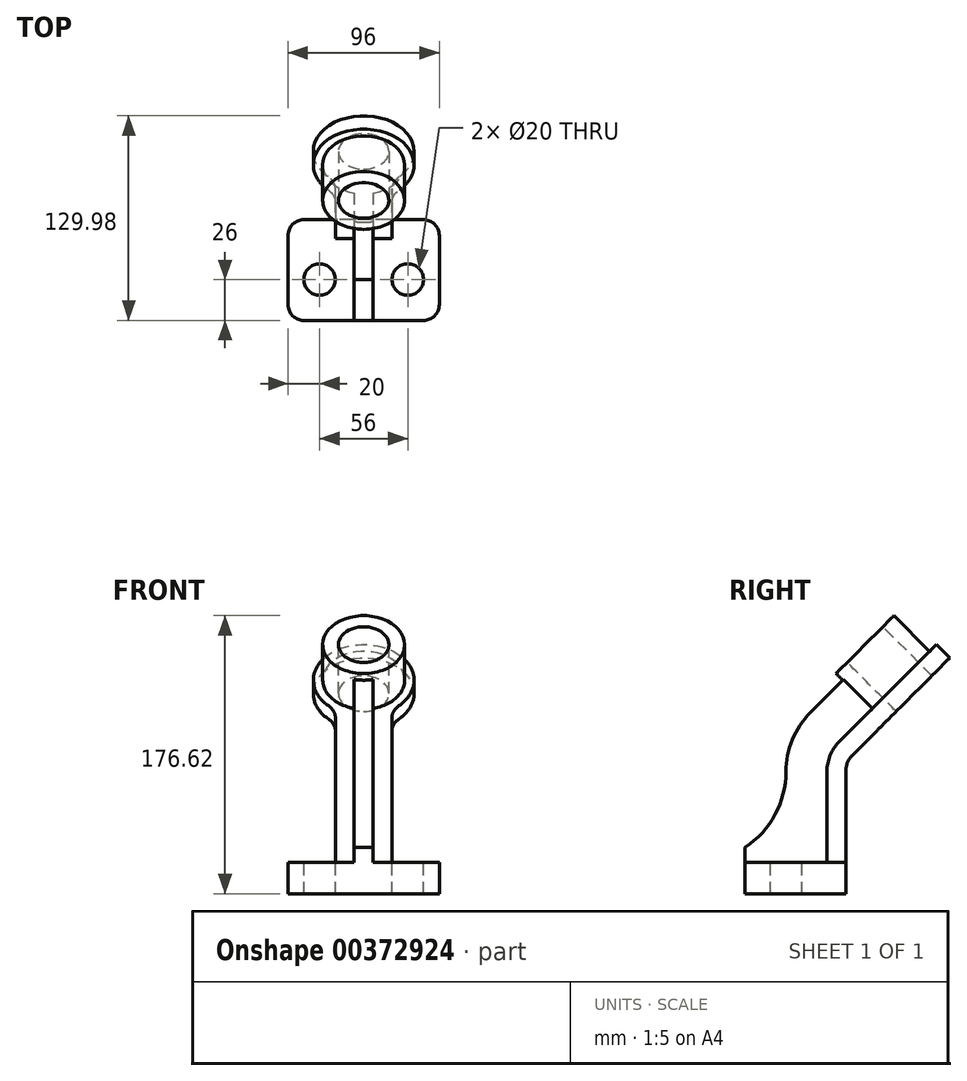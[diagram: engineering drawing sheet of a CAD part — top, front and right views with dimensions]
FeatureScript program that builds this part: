
annotation { "Feature Type Name" : "Feature", "Feature Type Description" : "" }
export const myFeature = defineFeature(function(context is Context, id is Id, definition is map)
    precondition{}
    {
        {
            var Q0;
            Q0=qCreatedBy(makeId("Top.planeOp"),FACE);
            var sketch = newSketch(context, id + "F0", { "sketchPlane" : qUnion([Q0])});
            skLineSegment(sketch, "E0.bottom", {"start": v(48, -32) * mm, "end": v(-48, -32) * mm});
            skLineSegment(sketch, "E0.top", {"start": v(48, 32) * mm, "end": v(-48, 32) * mm});
            skLineSegment(sketch, "E0.left", {"start": v(48, -32) * mm, "end": v(48, 32) * mm});
            skLineSegment(sketch, "E0.right", {"start": v(-48, -32) * mm, "end": v(-48, 32) * mm});
            skPoint(sketch, "E0.middle", {"position": v(0, 0) * mm});
            skSolve(sketch);
        }
        {
            var Q0;
            Q0=makeQuery(id+"F0.imprint","IMPRINT",FACE,{"disambiguationData":[TD([[makeQuery(id+"F0.imprint","IMPRINT",EDGE,{"derivedFrom":sQuery(id+"F0.wireOp",EDGE,"E0.bottom")}),-1.0]])]});
            extrude(context, id + "F1", {"entities" : qUnion([Q0]), "depth" : 20 * mm});
        }
        {
            var Q0;
            Q0=makeQuery(id+"F1.opExtrude","CAP_FACE",FACE,{"disambiguationData":[OSD([sQuery(id+"F0.wireOp",EDGE,"E0.bottom"),sQuery(id+"F0.wireOp",EDGE,"E0.top"),sQuery(id+"F0.wireOp",EDGE,"E0.left"),sQuery(id+"F0.wireOp",EDGE,"E0.right")])],"isStart":false});
            var sketch = newSketch(context, id + "F2", { "sketchPlane" : qUnion([Q0])});
            skCircle(sketch, "E1", {"center": v(-28, -6) * mm, "radius": 10 * mm});
            skCircle(sketch, "E2.MirrorC", {"center": v(28, -6) * mm, "radius": 10 * mm});
            skSolve(sketch);
        }
        {
            var Q0;
            Q0 = qSketchRegion(id + "F2", true);
            extrude(context, id + "F3", {"entities" : qUnion([Q0]), "operationType" : NewBodyOperationType.REMOVE, "oppositeDirection" : true, "depth" : 25 * mm});
        }
        {
            var Q0;
            Q0=makeQuery(id+"F1.opExtrude","SWEPT_EDGE",EDGE,{"disambiguationData":[OSD([sQuery(id+"F0.wireOp",EDGE,"E0.bottom"),sQuery(id+"F0.wireOp",EDGE,"E0.left")])]});
            var Q1;
            Q1=makeQuery(id+"F1.opExtrude","SWEPT_EDGE",EDGE,{"disambiguationData":[OSD([sQuery(id+"F0.wireOp",EDGE,"E0.bottom"),sQuery(id+"F0.wireOp",EDGE,"E0.right")])]});
            fillet(context, id + "F4", {"entities" : qUnion([Q0, Q1]), "radius" : 10 * mm, "tangentPropagation" : true, "allowEdgeOverflow" : false});
        }
        {
            var Q0;
            Q0=makeQuery(id+"F1.opExtrude","SWEPT_EDGE",EDGE,{"disambiguationData":[OSD([sQuery(id+"F0.wireOp",EDGE,"E0.top"),sQuery(id+"F0.wireOp",EDGE,"E0.right")])]});
            var Q1;
            Q1=makeQuery(id+"F1.opExtrude","SWEPT_EDGE",EDGE,{"disambiguationData":[OSD([sQuery(id+"F0.wireOp",EDGE,"E0.top"),sQuery(id+"F0.wireOp",EDGE,"E0.left")])]});
            fillet(context, id + "F5", {"entities" : qUnion([Q0, Q1]), "radius" : 10 * mm, "tangentPropagation" : true, "allowEdgeOverflow" : false});
        }
        {
            var Q0;
            Q0=qCreatedBy(makeId("Right.planeOp"),FACE);
            var sketch = newSketch(context, id + "F6", { "sketchPlane" : qUnion([Q0])});
            skLineSegment(sketch, "E3.0", {"start": v(-32, 20) * mm, "end": v(-22, 20) * mm});
            skLineSegment(sketch, "E4.0", {"start": v(-22, 20) * mm, "end": v(22, 20) * mm});
            skLineSegment(sketch, "E5.0", {"start": v(22, 20) * mm, "end": v(32, 20) * mm});
            skLineSegment(sketch, "E6", {"start": v(-32, 0) * mm, "end": v(-32, 146) * mm, "construction": true});
            skLineSegment(sketch, "E7", {"start": v(-32, 146) * mm, "end": v(32, 146) * mm, "construction": true});
            skLineSegment(sketch, "E8", {"start": v(44.24, 158.24) * mm, "end": v(15.36, 129.36) * mm});
            skSolve(sketch);
        }
        {
            var Q0;
            Q0=sQuery(id+"F6.wireOp",EDGE,"E8");
            extrude(context, id + "F7", {"bodyType" : ToolBodyType.SURFACE, "surfaceEntities" : qUnion([Q0]), "endBound" : BoundingType.SYMMETRIC, "depth" : 62.6 * mm});
        }
        {
            var Q0;
            Q0=makeQuery(id+"F7.opExtrude","SWEPT_FACE",FACE,{"disambiguationData":[OSD([sQuery(id+"F6.wireOp",EDGE,"E8")])]});
            cPlane(context, id + "F8", {"entities" : qUnion([Q0]), "cplaneType" : CPlaneType.OFFSET, "offset" : 0 * mm, "width" : 150 * mm, "height" : 150 * mm});
        }
        {
            var Q0;
            Q0=qCreatedBy(id+"F8.planeOp",FACE);
            var sketch = newSketch(context, id + "F9", { "sketchPlane" : qUnion([Q0])});
            skCircle(sketch, "E9", {"center": v(0, 143.17) * mm, "radius": 26 * mm});
            skCircle(sketch, "E10", {"center": v(0, 143.17) * mm, "radius": 16 * mm});
            skSolve(sketch);
        }
        {
            var Q0;
            Q0 = qSketchRegion(id + "F9", true);
            extrude(context, id + "F10", {"entities" : qUnion([Q0]), "oppositeDirection" : true, "depth" : 32 * mm});
        }
        {
            var Q0;
            Q0=makeQuery(id+"F10.opExtrude","CAP_FACE",FACE,{"disambiguationData":[OSD([sQuery(id+"F9.wireOp",EDGE,"E9"),sQuery(id+"F9.wireOp",EDGE,"E10")])],"isStart":false});
            var sketch = newSketch(context, id + "F11", { "sketchPlane" : qUnion([Q0])});
            skCircle(sketch, "E11", {"center": v(0, 143.17) * mm, "radius": 32 * mm});
            skSolve(sketch);
        }
        {
            var Q0;
            Q0=makeQuery(id+"F11.imprint","IMPRINT",FACE,{"disambiguationData":[TD([[makeQuery(id+"F11.imprint","IMPRINT",EDGE,{"derivedFrom":sQuery(id+"F11.wireOp",EDGE,"E11")}),1.0]])]});
            var Q1;
            Q1=makeQuery(id+"F11.imprint","IMPRINT",FACE,{"disambiguationData":[TD([[makeQuery(id+"F11.imprint","IMPRINT",EDGE,{"derivedFrom":makeQuery(id+"F10.opExtrude","CAP_EDGE",EDGE,{"disambiguationData":[OSD([sQuery(id+"F9.wireOp",EDGE,"E9")])],"isStart":false})}),-1.0]])]});
            extrude(context, id + "F12", {"entities" : qUnion([Q0, Q1]), "operationType" : NewBodyOperationType.ADD, "depth" : 12 * mm});
        }
        {
            var Q0;
            Q0=qCreatedBy(makeId("Right.planeOp"),FACE);
            var sketch = newSketch(context, id + "F13", { "sketchPlane" : qUnion([Q0])});
            skLineSegment(sketch, "E12.0", {"start": v(22, 20) * mm, "end": v(32, 20) * mm});
            skLineSegment(sketch, "E13.0", {"start": v(97.98, 149.75) * mm, "end": v(52.72, 104.5) * mm});
            skLineSegment(sketch, "E14.0", {"start": v(89.5, 158.24) * mm, "end": v(44.24, 112.98) * mm});
            skLineSegment(sketch, "E15", {"start": v(32, 77.56) * mm, "end": v(32, 0) * mm});
            skArc(sketch, "E16.filletArc", {"start": v(36.4, 88.17) * mm, "mid": v(33.14, 83.3) * mm, "end": v(32, 77.56) * mm});
            skLineSegment(sketch, "E17.0", {"start": v(20, 77.56) * mm, "end": v(20, 0) * mm});
            skArc(sketch, "E18", {"start": v(27.9, 96.65) * mm, "mid": v(22.06, 87.9) * mm, "end": v(20, 77.56) * mm});
            skLineSegment(sketch, "E19", {"start": v(20, 0) * mm, "end": v(32, 0) * mm});
            skLineSegment(sketch, "E20", {"start": v(36.4, 88.17) * mm, "end": v(57.1, 108.88) * mm});
            skLineSegment(sketch, "E21", {"start": v(57.1, 108.88) * mm, "end": v(48.62, 117.37) * mm});
            skLineSegment(sketch, "E22", {"start": v(48.62, 117.37) * mm, "end": v(27.9, 96.65) * mm});
            skSolve(sketch);
        }
        {
            var Q0;
            Q0 = qSketchRegion(id + "F13", true);
            extrude(context, id + "F14", {"entities" : qUnion([Q0]), "endBound" : BoundingType.SYMMETRIC, "depth" : 36 * mm});
        }
        {
            var Q0;
            Q0=makeQuery(id+"F14.opExtrude","SWEPT_BODY",BODY,{"disambiguationData":[OSD([sQuery(id+"F13.wireOp",EDGE,"E15"),sQuery(id+"F13.wireOp",EDGE,"E16.filletArc"),sQuery(id+"F13.wireOp",EDGE,"E17.0"),sQuery(id+"F13.wireOp",EDGE,"E18"),sQuery(id+"F13.wireOp",EDGE,"E19"),sQuery(id+"F13.wireOp",EDGE,"E20"),sQuery(id+"F13.wireOp",EDGE,"E21"),sQuery(id+"F13.wireOp",EDGE,"E22")])]});
            var Q1;
            Q1=makeQuery(id+"F10.opExtrude","SWEPT_BODY",BODY,{"disambiguationData":[OSD([sQuery(id+"F9.wireOp",EDGE,"E9"),sQuery(id+"F9.wireOp",EDGE,"E10")])]});
            var Q2;
            Q2=makeQuery(id+"F1.opExtrude","SWEPT_BODY",BODY,{"disambiguationData":[OSD([sQuery(id+"F0.wireOp",EDGE,"E0.bottom"),sQuery(id+"F0.wireOp",EDGE,"E0.top"),sQuery(id+"F0.wireOp",EDGE,"E0.left"),sQuery(id+"F0.wireOp",EDGE,"E0.right")])]});
            booleanBodies(context, id + "F15", {"operationType" : BooleanOperationType.UNION, "tools" : qUnion([Q0, Q1, Q2])});
        }
        {
            var Q0;
            Q0=qCreatedBy(makeId("Right.planeOp"),FACE);
            var sketch = newSketch(context, id + "F16", { "sketchPlane" : qUnion([Q0])});
            skLineSegment(sketch, "E23.0", {"start": v(33.54, 139.06) * mm, "end": v(9.52, 115.04) * mm});
            skLineSegment(sketch, "E24.0", {"start": v(-6, 20) * mm, "end": v(-6, 0) * mm});
            skArc(sketch, "E25", {"start": v(9.52, 115.04) * mm, "mid": v(-1.97, 97.84) * mm, "end": v(-6, 77.56) * mm});
            skLineSegment(sketch, "E26", {"start": v(-32, 20) * mm, "end": v(65.9, 20) * mm});
            skArc(sketch, "E27", {"start": v(-32, 29.42) * mm, "mid": v(-12.92, 50.2) * mm, "end": v(-6, 77.56) * mm});
            skLineSegment(sketch, "E28.0", {"start": v(-32, 0) * mm, "end": v(-32, 29.42) * mm});
            skPoint(sketch, "E29.orphan", {"position": v(-32, 146) * mm});
            skLineSegment(sketch, "E30", {"start": v(33.54, 139.06) * mm, "end": v(51.93, 120.67) * mm});
            skLineSegment(sketch, "E31.0", {"start": v(48.62, 117.37) * mm, "end": v(27.9, 96.65) * mm});
            skArc(sketch, "E32.0", {"start": v(27.9, 96.65) * mm, "mid": v(22.06, 87.9) * mm, "end": v(20, 77.56) * mm});
            skLineSegment(sketch, "E33.0", {"start": v(20, 77.56) * mm, "end": v(20, 0) * mm});
            skLineSegment(sketch, "E34", {"start": v(51.93, 120.67) * mm, "end": v(48.62, 117.37) * mm});
            skSolve(sketch);
        }
        {
            var Q0;
            Q0=makeQuery(id+"F16.imprint","IMPRINT",FACE,{"disambiguationData":[TD([[makeQuery(id+"F16.imprint","IMPRINT",EDGE,{"derivedFrom":sQuery(id+"F16.wireOp",EDGE,"E23.0")}),1.0]])]});
            extrude(context, id + "F17", {"entities" : qUnion([Q0]), "operationType" : NewBodyOperationType.ADD, "endBound" : BoundingType.SYMMETRIC, "depth" : 12 * mm});
        }
        {
            var Q0;
            Q0=makeQuery(id+"F15.opBoolean","INTERSECT",EDGE,{"derivedFrom":[makeQuery(id+"F12.opExtrude","SWEPT_FACE",FACE,{"disambiguationData":[OSD([sQuery(id+"F11.wireOp",EDGE,"E11")])]}),makeQuery(id+"F14.opExtrude","CAP_FACE",FACE,{"disambiguationData":[OSD([sQuery(id+"F13.wireOp",EDGE,"E15"),sQuery(id+"F13.wireOp",EDGE,"E16.filletArc"),sQuery(id+"F13.wireOp",EDGE,"E17.0"),sQuery(id+"F13.wireOp",EDGE,"E18"),sQuery(id+"F13.wireOp",EDGE,"E19"),sQuery(id+"F13.wireOp",EDGE,"E20"),sQuery(id+"F13.wireOp",EDGE,"E21"),sQuery(id+"F13.wireOp",EDGE,"E22")])],"isStart":false})]});
            var Q1;
            Q1=makeQuery(id+"F15.opBoolean","INTERSECT",EDGE,{"derivedFrom":[makeQuery(id+"F12.opExtrude","SWEPT_FACE",FACE,{"disambiguationData":[OSD([sQuery(id+"F11.wireOp",EDGE,"E11")])]}),makeQuery(id+"F14.opExtrude","CAP_FACE",FACE,{"disambiguationData":[OSD([sQuery(id+"F13.wireOp",EDGE,"E15"),sQuery(id+"F13.wireOp",EDGE,"E16.filletArc"),sQuery(id+"F13.wireOp",EDGE,"E17.0"),sQuery(id+"F13.wireOp",EDGE,"E18"),sQuery(id+"F13.wireOp",EDGE,"E19"),sQuery(id+"F13.wireOp",EDGE,"E20"),sQuery(id+"F13.wireOp",EDGE,"E21"),sQuery(id+"F13.wireOp",EDGE,"E22")])],"isStart":true})]});
            fillet(context, id + "F18", {"entities" : qUnion([Q0, Q1]), "radius" : 15 * mm, "tangentPropagation" : true, "allowEdgeOverflow" : false});
        }
    });
